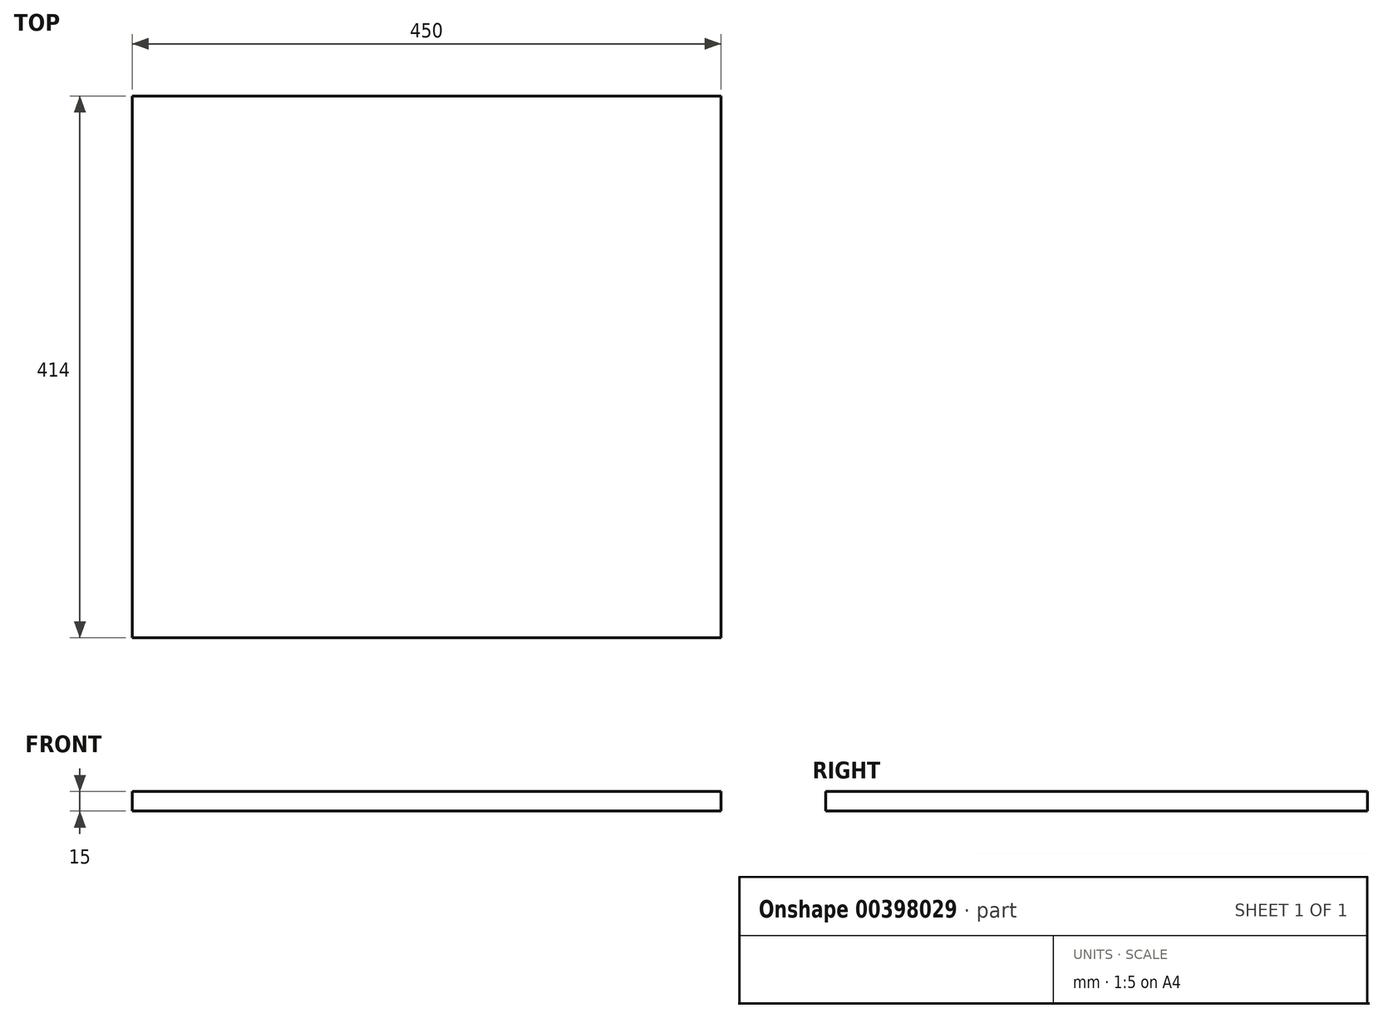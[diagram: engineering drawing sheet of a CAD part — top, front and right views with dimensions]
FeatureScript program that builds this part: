
annotation { "Feature Type Name" : "Feature", "Feature Type Description" : "" }
export const myFeature = defineFeature(function(context is Context, id is Id, definition is map)
    precondition{}
    {
        {
            var Q0;
            Q0=qCreatedBy(makeId("Top.planeOp"),FACE);
            var sketch = newSketch(context, id + "F0", { "sketchPlane" : qUnion([Q0])});
            skLineSegment(sketch, "E0.bottom", {"start": v(225, -207) * mm, "end": v(-225, -207) * mm});
            skLineSegment(sketch, "E0.top", {"start": v(225, 207) * mm, "end": v(-225, 207) * mm});
            skLineSegment(sketch, "E0.left", {"start": v(225, -207) * mm, "end": v(225, 207) * mm});
            skLineSegment(sketch, "E0.right", {"start": v(-225, -207) * mm, "end": v(-225, 207) * mm});
            skPoint(sketch, "E0.middle", {"position": v(0, 0) * mm});
            skSolve(sketch);
        }
        {
            var Q0;
            Q0 = qSketchRegion(id + "F0", true);
            extrude(context, id + "F1", {"entities" : qUnion([Q0]), "depth" : 15 * mm});
        }
    });
